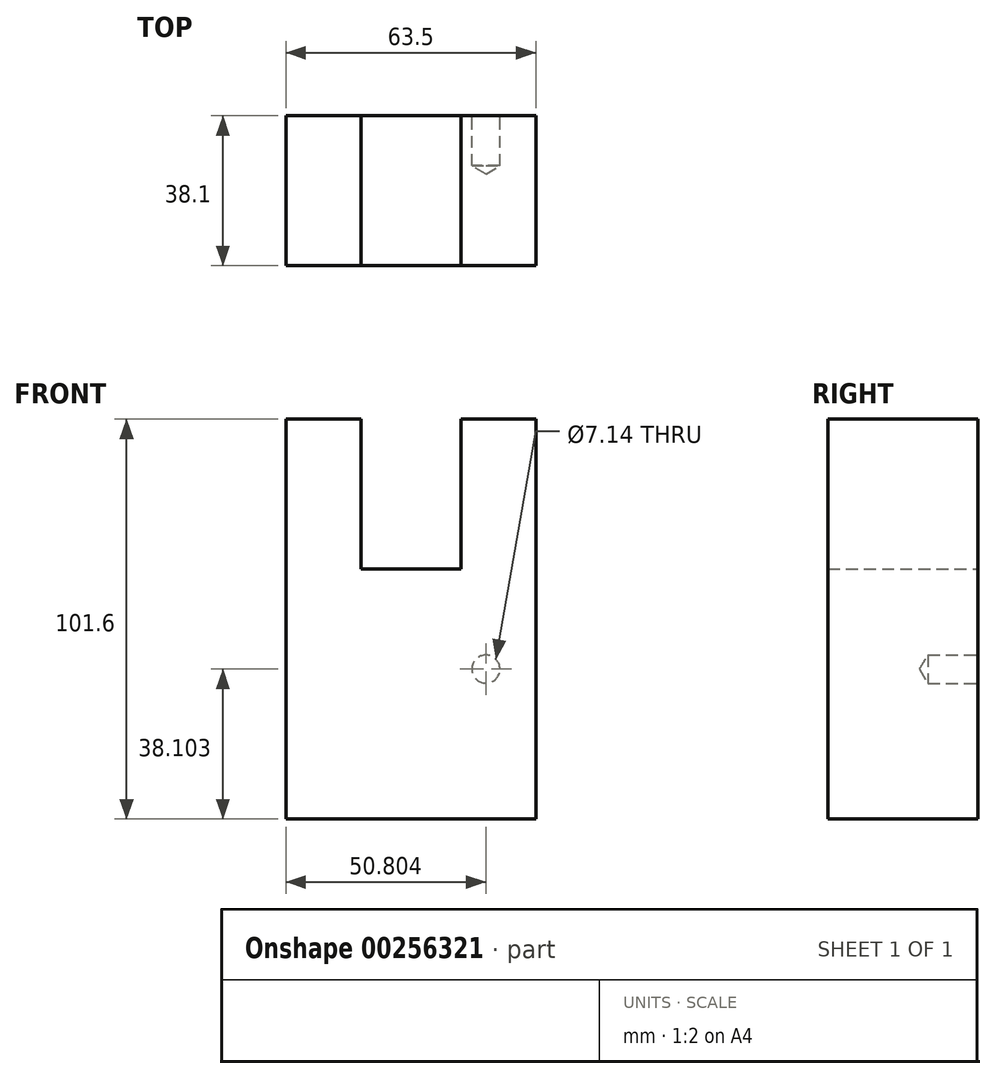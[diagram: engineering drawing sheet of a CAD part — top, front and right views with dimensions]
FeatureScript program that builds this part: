
annotation { "Feature Type Name" : "Feature", "Feature Type Description" : "" }
export const myFeature = defineFeature(function(context is Context, id is Id, definition is map)
    precondition{}
    {
        {
            var Q0;
            Q0=qCreatedBy(makeId("Front.planeOp"),FACE);
            var sketch = newSketch(context, id + "F0", { "sketchPlane" : qUnion([Q0])});
            skLineSegment(sketch, "E0", {"start": v(-40.86, -56.49) * mm, "end": v(22.64, -56.49) * mm});
            skLineSegment(sketch, "E1", {"start": v(22.64, -56.49) * mm, "end": v(22.64, 45.11) * mm});
            skLineSegment(sketch, "E2", {"start": v(22.64, 45.11) * mm, "end": v(3.6, 45.11) * mm});
            skLineSegment(sketch, "E3", {"start": v(3.6, 45.11) * mm, "end": v(3.6, 7.01) * mm});
            skLineSegment(sketch, "E4", {"start": v(3.6, 7.01) * mm, "end": v(-21.8, 7.01) * mm});
            skLineSegment(sketch, "E5", {"start": v(-21.8, 7.01) * mm, "end": v(-21.8, 45.11) * mm});
            skLineSegment(sketch, "E6", {"start": v(-40.86, -56.49) * mm, "end": v(-40.86, 45.11) * mm});
            skLineSegment(sketch, "E7", {"start": v(-40.86, 45.11) * mm, "end": v(-21.8, 45.11) * mm});
            skSolve(sketch);
        }
        {
            var Q0;
            Q0=makeQuery(id+"F0.imprint","IMPRINT",FACE,{"disambiguationData":[TD([[makeQuery(id+"F0.imprint","IMPRINT",EDGE,{"derivedFrom":sQuery(id+"F0.wireOp",EDGE,"E0")}),1.0]])]});
            extrude(context, id + "F1", {"entities" : qUnion([Q0]), "depth" : 38.1 * mm});
        }
        {
            var Q0;
            Q0=makeQuery(id+"F1.opExtrude","CAP_FACE",FACE,{"disambiguationData":[OSD([sQuery(id+"F0.wireOp",EDGE,"E0"),sQuery(id+"F0.wireOp",EDGE,"E1"),sQuery(id+"F0.wireOp",EDGE,"E2"),sQuery(id+"F0.wireOp",EDGE,"E3"),sQuery(id+"F0.wireOp",EDGE,"E4"),sQuery(id+"F0.wireOp",EDGE,"E5"),sQuery(id+"F0.wireOp",EDGE,"E6"),sQuery(id+"F0.wireOp",EDGE,"E7")])],"isStart":true});
            var sketch = newSketch(context, id + "F2", { "sketchPlane" : qUnion([Q0])});
            skLineSegment(sketch, "E8", {"start": v(-22.64, -56.49) * mm, "end": v(-9.94, -56.49) * mm});
            skLineSegment(sketch, "E9", {"start": v(-9.94, -56.49) * mm, "end": v(-9.94, -18.39) * mm});
            skSolve(sketch);
        }
        {
            var Q0;
            Q0=sQuery(id+"F2.wireOp",VERTEX,"E9.end");
            var Q1;
            Q1=makeQuery(id+"F1.opExtrude","SWEPT_BODY",BODY,{"disambiguationData":[OSD([sQuery(id+"F0.wireOp",EDGE,"E0"),sQuery(id+"F0.wireOp",EDGE,"E1"),sQuery(id+"F0.wireOp",EDGE,"E2"),sQuery(id+"F0.wireOp",EDGE,"E3"),sQuery(id+"F0.wireOp",EDGE,"E4"),sQuery(id+"F0.wireOp",EDGE,"E5"),sQuery(id+"F0.wireOp",EDGE,"E6"),sQuery(id+"F0.wireOp",EDGE,"E7")])]});
            hole(context, id + "F3", {"style" : HoleStyle.SIMPLE, "endStyle" : HoleEndStyle.BLIND, "holeDiameter" : 7.14 * mm, "holeDepth" : 12.7 * mm, "tappedDepth" : 12.7 * mm, "tapClearance" : 3, "locations" : qUnion([Q0]), "scope" : qUnion([Q1])});
        }
    });
